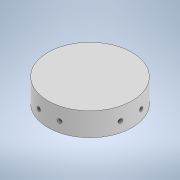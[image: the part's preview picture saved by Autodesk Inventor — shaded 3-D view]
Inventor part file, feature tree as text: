
AUTODESK INVENTOR PART (.ipt)
format: ipt  version: 2021 (Build 250183000, 183)  size: 149,504 bytes
history: native  units: mm
features: extrude x4, sketch x4, other x1
ambient origin geometry x8: Origin, YZ Plane, XZ Plane, XY Plane, X Axis, Y Axis, Z Axis, Center Point
bodies: Body1 (feature_tree)
feature tree (9):
  other  "Sólido1"
  extrude  "Extrusión1"  Depth=22.5mm
  extrude  "Extrusión2"  Depth=32.0mm
  extrude  "Extrusión3"  Depth=15.0mm TaperAngle=0.0deg
  extrude  "Extrusión4"  Depth=3.0mm
  sketch  "Boceto1"  dims[d0=65.0mm d1=22.5mm]
  sketch  "Boceto2"  dims[d3=16.0mm d4=32.0mm]
  sketch  "Boceto3"  dims[d5=40.0mm d7=360.0deg d9=15.0mm d10=0.0mm]
  sketch  "Boceto4"  dims[d11=8.0mm d12=8.0mm d13=16.0mm d15=3.0mm d16=3.0mm d17=10200.0mm d18=0.0mm d19=8.0mm d20=8.0mm d21=16.0mm d22=3.0mm d23=3.0mm d24=10200.0mm d25=0.0mm d26=3.0mm d27=0.0mm]
